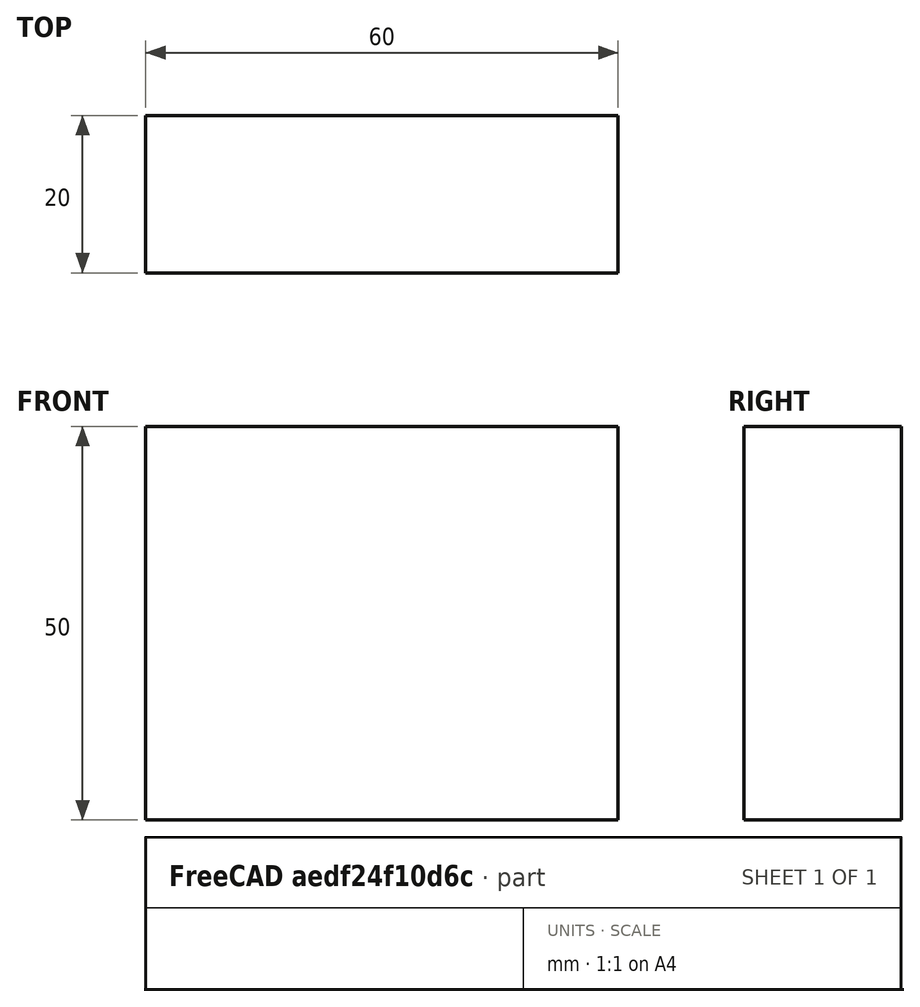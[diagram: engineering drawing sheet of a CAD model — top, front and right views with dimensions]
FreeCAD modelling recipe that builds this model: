
FCSTD DOCUMENT  (FreeCAD 0.15R4671 (Git))
Label: Flat Bar 60x20 EN10058 S235JR
License: All rights reserved
LicenseURL: http://en.wikipedia.org/wiki/All_rights_reserved
objects: Sketcher::SketchObject×1, Part::Extrusion×1
note: 2 computed .brp shape members not serialized (recipe doc carries the construction recipe); baked Part::Feature solids carry a one-line shape summary decoded from their .brp

FEATURE [Sketcher::SketchObject] Sketch
  sketch-geometry (4):
    g0: LineSegment StartX=-30 StartY=-10 StartZ=0 EndX=30 EndY=-10 EndZ=0
    g1: LineSegment StartX=30 StartY=-10 StartZ=0 EndX=30 EndY=10 EndZ=0
    g2: LineSegment StartX=30 StartY=10 StartZ=0 EndX=-30 EndY=10 EndZ=0
    g3: LineSegment StartX=-30 StartY=10 StartZ=0 EndX=-30 EndY=-10 EndZ=0
  constraints (12):
    c: Coincident(g0,g1)
    c: Coincident(g1,g2)
    c: Coincident(g2,g3)
    c: Coincident(g3,g0)
    c: Horizontal(g0)
    c: Horizontal(g2)
    c: Vertical(g1)
    c: Vertical(g3)
    c: Symmetric(g1,g2,g-2)
    c: Symmetric(g0,g1,g-1)
    c: DistanceY(g1) = 20
    c: DistanceX(g0) = 60
FEATURE [Part::Extrusion] Extrude  label="Flat Bar 60x20 EN10058 S235JR"
  Base = -> Sketch
  Dir = (0,0,50)
  Solid = true
